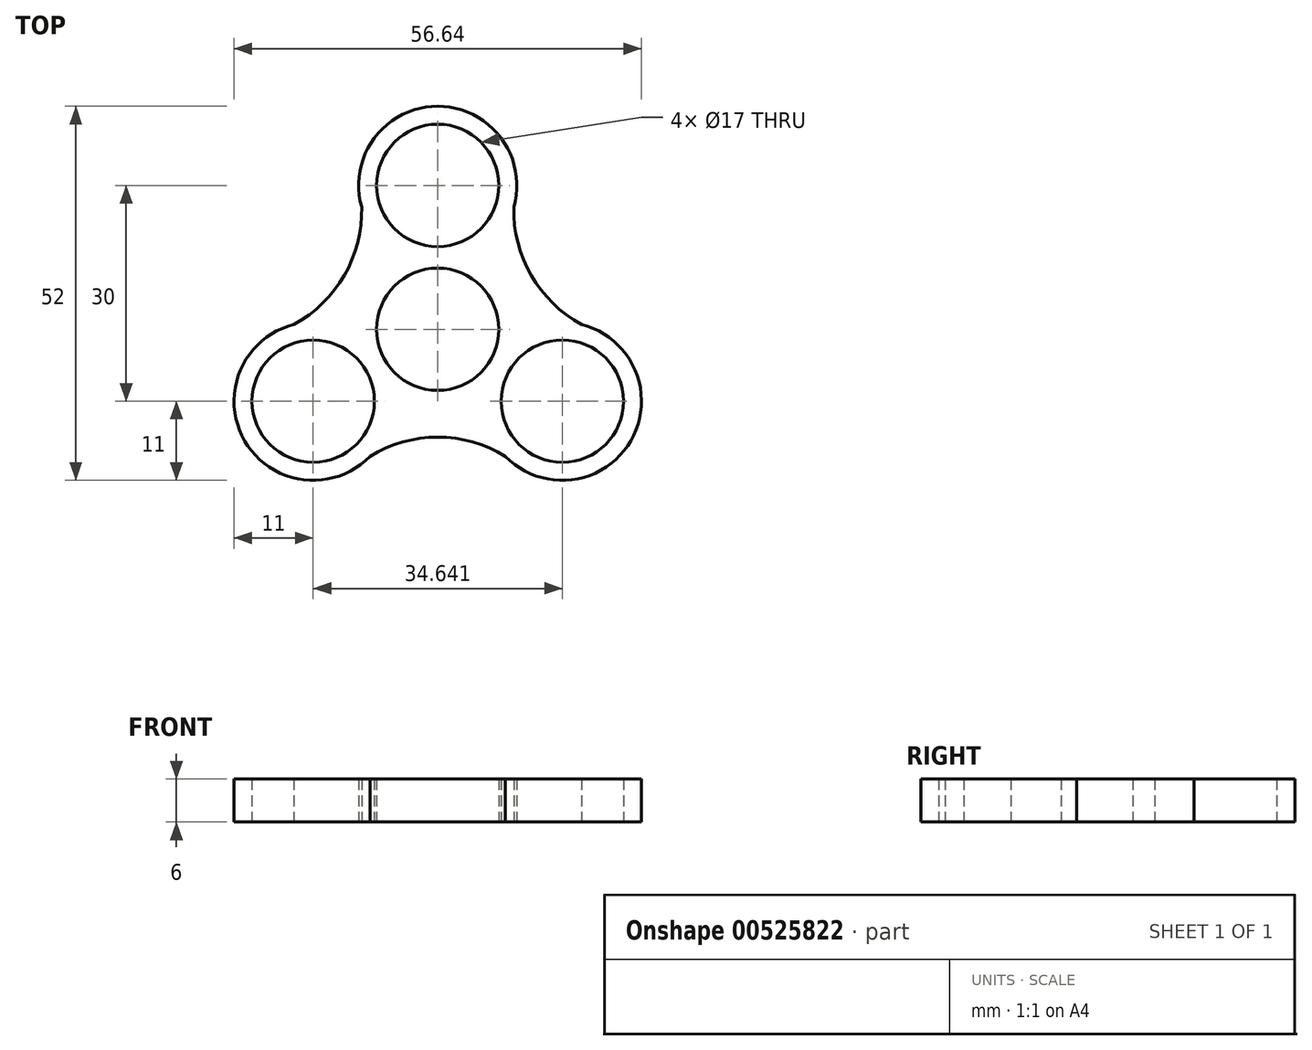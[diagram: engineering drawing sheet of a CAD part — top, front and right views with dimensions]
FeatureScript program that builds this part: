
annotation { "Feature Type Name" : "Feature", "Feature Type Description" : "" }
export const myFeature = defineFeature(function(context is Context, id is Id, definition is map)
    precondition{}
    {
        {
            var Q0;
            Q0=qCreatedBy(makeId("Top.planeOp"),FACE);
            var sketch = newSketch(context, id + "F0", { "sketchPlane" : qUnion([Q0])});
            skCircle(sketch, "E0", {"center": v(0, 0) * mm, "radius": 8.5 * mm});
            skCircle(sketch, "E1", {"center": v(0, 0) * mm, "radius": 15 * mm, "construction": true});
            skCircle(sketch, "E2", {"center": v(0, 0) * mm, "radius": 20 * mm, "construction": true});
            skCircle(sketch, "E3", {"center": v(0, 20) * mm, "radius": 8.5 * mm});
            skArc(sketch, "E4", {"start": v(-10.58, 16.98) * mm, "mid": v(0, 31) * mm, "end": v(10.58, 16.98) * mm});
            skCircle(sketch, "E5.1.0", {"center": v(-17.32, -10) * mm, "radius": 8.5 * mm});
            skArc(sketch, "E5.1.1", {"start": v(-9.41, -17.65) * mm, "mid": v(-26.85, -15.5) * mm, "end": v(-19.99, 0.67) * mm});
            skCircle(sketch, "E5.2.0", {"center": v(17.32, -10) * mm, "radius": 8.5 * mm});
            skArc(sketch, "E5.2.1", {"start": v(19.99, 0.67) * mm, "mid": v(26.85, -15.5) * mm, "end": v(9.41, -17.65) * mm});
            skArc(sketch, "E6", {"start": v(-19.99, 0.67) * mm, "mid": v(-13, 7.5) * mm, "end": v(-10.58, 16.97) * mm});
            skArc(sketch, "E7", {"start": v(9.41, -17.65) * mm, "mid": v(0, -15) * mm, "end": v(-9.41, -17.65) * mm});
            skArc(sketch, "E8", {"start": v(10.58, 16.97) * mm, "mid": v(13, 7.5) * mm, "end": v(19.99, 0.67) * mm});
            skSolve(sketch);
        }
        {
            var Q0;
            Q0=makeQuery(id+"F0.imprint","IMPRINT",FACE,{"disambiguationData":[TD([[makeQuery(id+"F0.imprint","IMPRINT",EDGE,{"derivedFrom":sQuery(id+"F0.wireOp",EDGE,"E0")}),-1.0]])]});
            extrude(context, id + "F1", {"entities" : qUnion([Q0]), "depth" : 6 * mm, "offsetDistance" : 25 * mm});
        }
    });
